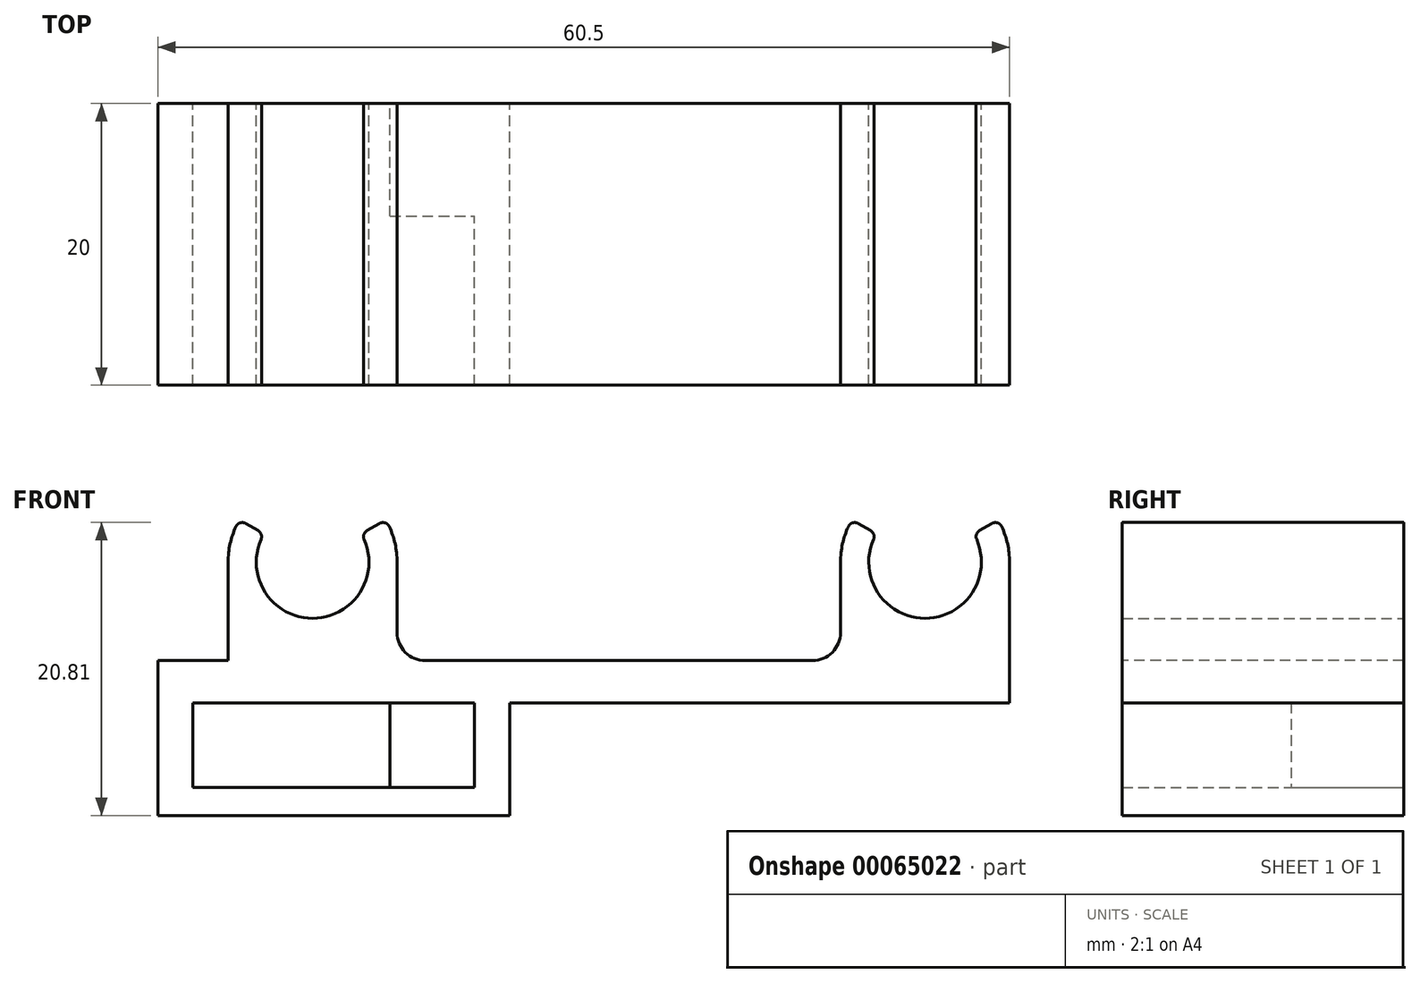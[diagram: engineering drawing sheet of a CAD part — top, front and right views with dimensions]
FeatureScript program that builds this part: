
annotation { "Feature Type Name" : "Feature", "Feature Type Description" : "" }
export const myFeature = defineFeature(function(context is Context, id is Id, definition is map)
    precondition{}
    {
        {
            var Q0;
            Q0=qCreatedBy(makeId("Top.planeOp"),FACE);
            var sketch = newSketch(context, id + "F0", { "sketchPlane" : qUnion([Q0])});
            skLineSegment(sketch, "E0.rect.bottom", {"start": v(-27.25, 10) * mm, "end": v(27.25, 10) * mm});
            skLineSegment(sketch, "E0.rect.top", {"start": v(-27.25, -10) * mm, "end": v(27.25, -10) * mm});
            skLineSegment(sketch, "E0.rect.left", {"start": v(-27.25, 10) * mm, "end": v(-27.25, -10) * mm});
            skLineSegment(sketch, "E0.rect.right", {"start": v(27.25, 10) * mm, "end": v(27.25, -10) * mm});
            skPoint(sketch, "E0.rect.middle", {"position": v(0, 0) * mm});
            skSolve(sketch);
        }
        {
            var Q0;
            Q0=makeQuery(id+"F0.imprint","IMPRINT",FACE,{"disambiguationData":[TD([[makeQuery(id+"F0.imprint","IMPRINT",EDGE,{"derivedFrom":sQuery(id+"F0.wireOp",EDGE,"E0.rect.bottom")}),-1.0]])]});
            extrude(context, id + "F1", {"entities" : qUnion([Q0]), "depth" : 3 * mm});
        }
        {
            var Q0;
            Q0=qCreatedBy(makeId("Front.planeOp"),FACE);
            var sketch = newSketch(context, id + "F2", { "sketchPlane" : qUnion([Q0])});
            skArc(sketch, "E1", {"start": v(-15.75, 10) * mm, "mid": v(-15.95, 11.55) * mm, "end": v(-16.55, 13) * mm});
            skArc(sketch, "E2", {"start": v(-25.21, 12) * mm, "mid": v(-21.75, 6) * mm, "end": v(-18.29, 12) * mm});
            skLineSegment(sketch, "E3", {"start": v(-27.75, 0) * mm, "end": v(-27.75, 10) * mm});
            skLineSegment(sketch, "E4", {"start": v(-15.75, 10) * mm, "end": v(-15.75, 0) * mm});
            skLineSegment(sketch, "E5", {"start": v(-27.75, 0) * mm, "end": v(-15.75, 0) * mm});
            skLineSegment(sketch, "E6", {"start": v(-25.21, 12) * mm, "end": v(-26.95, 13) * mm});
            skLineSegment(sketch, "E7", {"start": v(-18.29, 12) * mm, "end": v(-16.55, 13) * mm});
            skArc(sketch, "E8.trimOffspring", {"start": v(-26.95, 13) * mm, "mid": v(-27.55, 11.55) * mm, "end": v(-27.75, 10) * mm});
            skLineSegment(sketch, "E9.MirrorCS", {"start": v(18.29, 12) * mm, "end": v(16.55, 13) * mm});
            skLineSegment(sketch, "E10.MirrorCS", {"start": v(25.21, 12) * mm, "end": v(26.95, 13) * mm});
            skArc(sketch, "E11.MirrorCS", {"start": v(15.75, 10) * mm, "mid": v(15.95, 11.55) * mm, "end": v(16.55, 13) * mm});
            skArc(sketch, "E12.MirrorCS", {"start": v(26.95, 13) * mm, "mid": v(27.55, 11.55) * mm, "end": v(27.75, 10) * mm});
            skLineSegment(sketch, "E13.MirrorCS", {"start": v(27.75, 0) * mm, "end": v(15.75, 0) * mm});
            skLineSegment(sketch, "E14.MirrorCS", {"start": v(27.75, 0) * mm, "end": v(27.75, 10) * mm});
            skLineSegment(sketch, "E15.MirrorCS", {"start": v(15.75, 10) * mm, "end": v(15.75, 0) * mm});
            skArc(sketch, "E16.MirrorCS", {"start": v(25.21, 12) * mm, "mid": v(21.75, 6) * mm, "end": v(18.29, 12) * mm});
            skSolve(sketch);
        }
        {
            var Q0;
            Q0 = qSketchRegion(id + "F2", true);
            extrude(context, id + "F3", {"entities" : qUnion([Q0]), "operationType" : NewBodyOperationType.ADD, "endBound" : BoundingType.SYMMETRIC, "depth" : 20 * mm});
        }
        {
            var Q0;
            Q0=makeQuery(id+"F3.boolean.opBoolean","INTERSECT",EDGE,{"derivedFrom":[makeQuery(id+"F1.opExtrude","CAP_FACE",FACE,{"disambiguationData":[OSD([sQuery(id+"F0.wireOp",EDGE,"E0.rect.bottom"),sQuery(id+"F0.wireOp",EDGE,"E0.rect.top"),sQuery(id+"F0.wireOp",EDGE,"E0.rect.left"),sQuery(id+"F0.wireOp",EDGE,"E0.rect.right")])],"isStart":false}),makeQuery(id+"F3.opExtrude","SWEPT_FACE",FACE,{"disambiguationData":[OSD([sQuery(id+"F2.wireOp",EDGE,"E4")])]})]});
            var Q1;
            Q1=makeQuery(id+"F3.boolean.opBoolean","INTERSECT",EDGE,{"derivedFrom":[makeQuery(id+"F1.opExtrude","CAP_FACE",FACE,{"disambiguationData":[OSD([sQuery(id+"F0.wireOp",EDGE,"E0.rect.bottom"),sQuery(id+"F0.wireOp",EDGE,"E0.rect.top"),sQuery(id+"F0.wireOp",EDGE,"E0.rect.left"),sQuery(id+"F0.wireOp",EDGE,"E0.rect.right")])],"isStart":false}),makeQuery(id+"F3.opExtrude","SWEPT_FACE",FACE,{"disambiguationData":[OSD([sQuery(id+"F2.wireOp",EDGE,"E15.MirrorCS")])]})]});
            fillet(context, id + "F4", {"entities" : qUnion([Q0, Q1]), "radius" : 2 * mm, "tangentPropagation" : true, "allowEdgeOverflow" : false});
        }
        {
            var Q0;
            Q0=makeQuery(id+"F3.opExtrude","SWEPT_EDGE",EDGE,{"disambiguationData":[OSD([sQuery(id+"F2.wireOp",EDGE,"E6"),sQuery(id+"F2.wireOp",EDGE,"E8.trimOffspring")])]});
            var Q1;
            Q1=makeQuery(id+"F3.opExtrude","SWEPT_EDGE",EDGE,{"disambiguationData":[OSD([sQuery(id+"F2.wireOp",EDGE,"E2"),sQuery(id+"F2.wireOp",EDGE,"E6")])]});
            var Q2;
            Q2=makeQuery(id+"F3.opExtrude","SWEPT_EDGE",EDGE,{"disambiguationData":[OSD([sQuery(id+"F2.wireOp",EDGE,"E2"),sQuery(id+"F2.wireOp",EDGE,"E7")])]});
            var Q3;
            Q3=makeQuery(id+"F3.opExtrude","SWEPT_EDGE",EDGE,{"disambiguationData":[OSD([sQuery(id+"F2.wireOp",EDGE,"E1"),sQuery(id+"F2.wireOp",EDGE,"E7")])]});
            var Q4;
            Q4=makeQuery(id+"F3.opExtrude","SWEPT_EDGE",EDGE,{"disambiguationData":[OSD([sQuery(id+"F2.wireOp",EDGE,"E9.MirrorCS"),sQuery(id+"F2.wireOp",EDGE,"E16.MirrorCS")])]});
            var Q5;
            Q5=makeQuery(id+"F3.opExtrude","SWEPT_EDGE",EDGE,{"disambiguationData":[OSD([sQuery(id+"F2.wireOp",EDGE,"E9.MirrorCS"),sQuery(id+"F2.wireOp",EDGE,"E11.MirrorCS")])]});
            var Q6;
            Q6=makeQuery(id+"F3.opExtrude","SWEPT_EDGE",EDGE,{"disambiguationData":[OSD([sQuery(id+"F2.wireOp",EDGE,"E10.MirrorCS"),sQuery(id+"F2.wireOp",EDGE,"E16.MirrorCS")])]});
            var Q7;
            Q7=makeQuery(id+"F3.opExtrude","SWEPT_EDGE",EDGE,{"disambiguationData":[OSD([sQuery(id+"F2.wireOp",EDGE,"E10.MirrorCS"),sQuery(id+"F2.wireOp",EDGE,"E12.MirrorCS")])]});
            fillet(context, id + "F5", {"entities" : qUnion([Q0, Q1, Q2, Q3, Q4, Q5, Q6, Q7]), "radius" : .5 * mm, "tangentPropagation" : true, "allowEdgeOverflow" : false});
        }
        {
            var Q0;
            Q0=qCreatedBy(makeId("Front.planeOp"),FACE);
            var sketch = newSketch(context, id + "F6", { "sketchPlane" : qUnion([Q0])});
            skLineSegment(sketch, "E17.bottom", {"start": v(-7.75, 0) * mm, "end": v(-32.75, 0) * mm});
            skLineSegment(sketch, "E17.top", {"start": v(-7.75, -8) * mm, "end": v(-32.75, -8) * mm});
            skLineSegment(sketch, "E17.left", {"start": v(-7.75, 0) * mm, "end": v(-7.75, -8) * mm});
            skLineSegment(sketch, "E17.right", {"start": v(-32.75, 0) * mm, "end": v(-32.75, -8) * mm});
            skLineSegment(sketch, "E18.bottom", {"start": v(-30.25, 0) * mm, "end": v(-10.25, 0) * mm});
            skLineSegment(sketch, "E18.top", {"start": v(-30.25, -6) * mm, "end": v(-10.25, -6) * mm});
            skLineSegment(sketch, "E18.left", {"start": v(-30.25, 0) * mm, "end": v(-30.25, -6) * mm});
            skLineSegment(sketch, "E18.right", {"start": v(-10.25, 0) * mm, "end": v(-10.25, -6) * mm});
            skSolve(sketch);
        }
        {
            var Q0;
            Q0=makeQuery(id+"F6.imprint","IMPRINT",FACE,{"disambiguationData":[TD([[makeQuery(id+"F6.imprint","IMPRINT",EDGE,{"derivedFrom":sQuery(id+"F6.wireOp",EDGE,"E17.top")}),-1.0]])]});
            extrude(context, id + "F7", {"entities" : qUnion([Q0]), "operationType" : NewBodyOperationType.ADD, "endBound" : BoundingType.SYMMETRIC, "depth" : 20 * mm});
        }
        {
            var Q0;
            Q0=makeQuery(id+"F7.boolean.opBoolean","MERGE",FACE,{"derivedFrom":[makeQuery(id+"F3.boolean.opBoolean","MERGE",FACE,{"derivedFrom":[makeQuery(id+"F1.opExtrude","SWEPT_FACE",FACE,{"disambiguationData":[OSD([sQuery(id+"F0.wireOp",EDGE,"E0.rect.top")])]}),makeQuery(id+"F3.opExtrude","CAP_FACE",FACE,{"disambiguationData":[OSD([sQuery(id+"F2.wireOp",EDGE,"E1"),sQuery(id+"F2.wireOp",EDGE,"E2"),sQuery(id+"F2.wireOp",EDGE,"E3"),sQuery(id+"F2.wireOp",EDGE,"E4"),sQuery(id+"F2.wireOp",EDGE,"E5"),sQuery(id+"F2.wireOp",EDGE,"E6"),sQuery(id+"F2.wireOp",EDGE,"E7"),sQuery(id+"F2.wireOp",EDGE,"E8.trimOffspring")])],"isStart":false}),makeQuery(id+"F3.opExtrude","CAP_FACE",FACE,{"disambiguationData":[OSD([sQuery(id+"F2.wireOp",EDGE,"E9.MirrorCS"),sQuery(id+"F2.wireOp",EDGE,"E10.MirrorCS"),sQuery(id+"F2.wireOp",EDGE,"E11.MirrorCS"),sQuery(id+"F2.wireOp",EDGE,"E12.MirrorCS"),sQuery(id+"F2.wireOp",EDGE,"E13.MirrorCS"),sQuery(id+"F2.wireOp",EDGE,"E14.MirrorCS"),sQuery(id+"F2.wireOp",EDGE,"E15.MirrorCS"),sQuery(id+"F2.wireOp",EDGE,"E16.MirrorCS")])],"isStart":false})]}),makeQuery(id+"F7.opExtrude","CAP_FACE",FACE,{"disambiguationData":[OSD([sQuery(id+"F6.wireOp",EDGE,"E17.bottom"),sQuery(id+"F6.wireOp",EDGE,"E17.top"),sQuery(id+"F6.wireOp",EDGE,"E17.left"),sQuery(id+"F6.wireOp",EDGE,"E17.right"),sQuery(id+"F6.wireOp",EDGE,"E18.top"),sQuery(id+"F6.wireOp",EDGE,"E18.left"),sQuery(id+"F6.wireOp",EDGE,"E18.right")])],"isStart":false})]});
            var sketch = newSketch(context, id + "F8", { "sketchPlane" : qUnion([Q0])});
            skLineSegment(sketch, "E19.bottom", {"start": v(-27.75, 0) * mm, "end": v(-32.75, 0) * mm});
            skLineSegment(sketch, "E19.top", {"start": v(-27.75, 3) * mm, "end": v(-32.75, 3) * mm});
            skLineSegment(sketch, "E19.left", {"start": v(-27.75, 0) * mm, "end": v(-27.75, 3) * mm});
            skLineSegment(sketch, "E19.right", {"start": v(-32.75, 0) * mm, "end": v(-32.75, 3) * mm});
            skSolve(sketch);
        }
        {
            var Q0;
            Q0=makeQuery(id+"F8.imprint","IMPRINT",FACE,{"disambiguationData":[TD([[makeQuery(id+"F8.imprint","IMPRINT",EDGE,{"derivedFrom":sQuery(id+"F8.wireOp",EDGE,"E19.top")}),1.0]])]});
            extrude(context, id + "F9", {"entities" : qUnion([Q0]), "operationType" : NewBodyOperationType.ADD, "oppositeDirection" : true, "depth" : 20 * mm});
        }
        {
            var Q0;
            Q0=makeQuery(id+"F9.boolean.opBoolean","MERGE",FACE,{"derivedFrom":[makeQuery(id+"F7.boolean.opBoolean","MERGE",FACE,{"derivedFrom":[makeQuery(id+"F3.boolean.opBoolean","MERGE",FACE,{"derivedFrom":[makeQuery(id+"F1.opExtrude","SWEPT_FACE",FACE,{"disambiguationData":[OSD([sQuery(id+"F0.wireOp",EDGE,"E0.rect.bottom")])]}),makeQuery(id+"F3.opExtrude","CAP_FACE",FACE,{"disambiguationData":[OSD([sQuery(id+"F2.wireOp",EDGE,"E1"),sQuery(id+"F2.wireOp",EDGE,"E2"),sQuery(id+"F2.wireOp",EDGE,"E3"),sQuery(id+"F2.wireOp",EDGE,"E4"),sQuery(id+"F2.wireOp",EDGE,"E5"),sQuery(id+"F2.wireOp",EDGE,"E6"),sQuery(id+"F2.wireOp",EDGE,"E7"),sQuery(id+"F2.wireOp",EDGE,"E8.trimOffspring")])],"isStart":true}),makeQuery(id+"F3.opExtrude","CAP_FACE",FACE,{"disambiguationData":[OSD([sQuery(id+"F2.wireOp",EDGE,"E9.MirrorCS"),sQuery(id+"F2.wireOp",EDGE,"E10.MirrorCS"),sQuery(id+"F2.wireOp",EDGE,"E11.MirrorCS"),sQuery(id+"F2.wireOp",EDGE,"E12.MirrorCS"),sQuery(id+"F2.wireOp",EDGE,"E13.MirrorCS"),sQuery(id+"F2.wireOp",EDGE,"E14.MirrorCS"),sQuery(id+"F2.wireOp",EDGE,"E15.MirrorCS"),sQuery(id+"F2.wireOp",EDGE,"E16.MirrorCS")])],"isStart":true})]}),makeQuery(id+"F7.opExtrude","CAP_FACE",FACE,{"disambiguationData":[OSD([sQuery(id+"F6.wireOp",EDGE,"E17.bottom"),sQuery(id+"F6.wireOp",EDGE,"E17.top"),sQuery(id+"F6.wireOp",EDGE,"E17.left"),sQuery(id+"F6.wireOp",EDGE,"E17.right"),sQuery(id+"F6.wireOp",EDGE,"E18.top"),sQuery(id+"F6.wireOp",EDGE,"E18.left"),sQuery(id+"F6.wireOp",EDGE,"E18.right")])],"isStart":true})]}),makeQuery(id+"F9.opExtrude","CAP_FACE",FACE,{"disambiguationData":[OSD([sQuery(id+"F8.wireOp",EDGE,"E19.bottom"),sQuery(id+"F8.wireOp",EDGE,"E19.top"),sQuery(id+"F8.wireOp",EDGE,"E19.left"),sQuery(id+"F8.wireOp",EDGE,"E19.right")])],"isStart":false})]});
            var sketch = newSketch(context, id + "F10", { "sketchPlane" : qUnion([Q0])});
            skLineSegment(sketch, "E20.bottom", {"start": v(10.25, 0) * mm, "end": v(16.25, 0) * mm});
            skLineSegment(sketch, "E20.top", {"start": v(10.25, -6) * mm, "end": v(16.25, -6) * mm});
            skLineSegment(sketch, "E20.left", {"start": v(10.25, 0) * mm, "end": v(10.25, -6) * mm});
            skLineSegment(sketch, "E20.right", {"start": v(16.25, 0) * mm, "end": v(16.25, -6) * mm});
            skSolve(sketch);
        }
        {
            var Q0;
            Q0=makeQuery(id+"F10.imprint","IMPRINT",FACE,{"disambiguationData":[TD([[makeQuery(id+"F10.imprint","IMPRINT",EDGE,{"derivedFrom":sQuery(id+"F10.wireOp",EDGE,"E20.bottom")}),1.0]])]});
            extrude(context, id + "F11", {"entities" : qUnion([Q0]), "operationType" : NewBodyOperationType.ADD, "oppositeDirection" : true, "depth" : 8 * mm});
        }
    });
